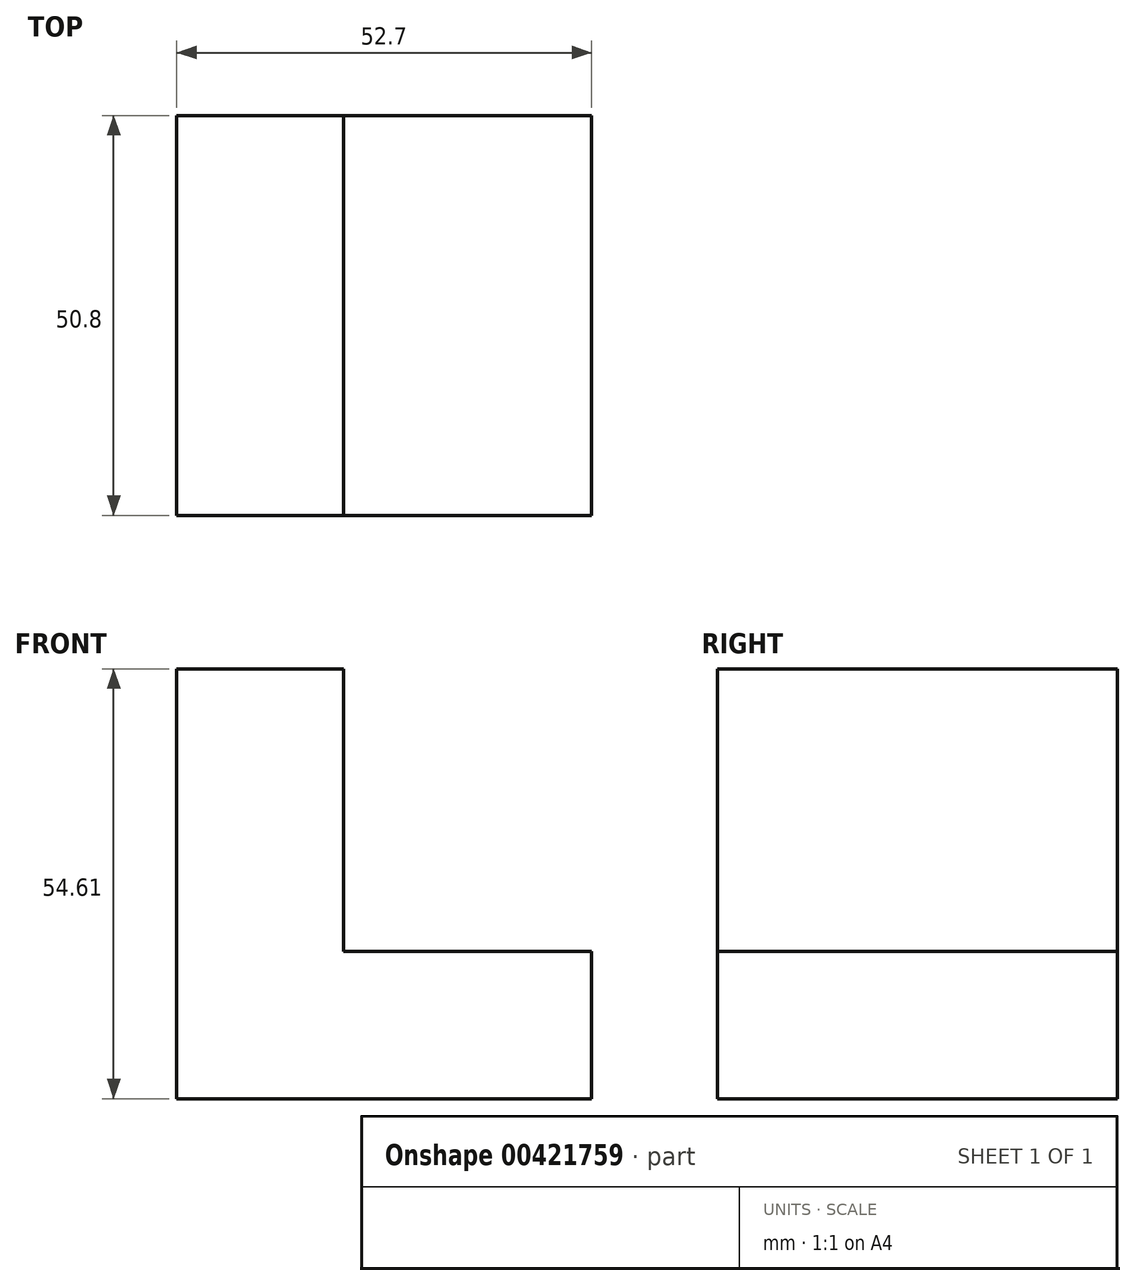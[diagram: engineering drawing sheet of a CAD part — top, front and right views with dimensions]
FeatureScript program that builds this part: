
annotation { "Feature Type Name" : "Feature", "Feature Type Description" : "" }
export const myFeature = defineFeature(function(context is Context, id is Id, definition is map)
    precondition{}
    {
        {
            var Q0;
            Q0=qCreatedBy(makeId("Front.planeOp"),FACE);
            var sketch = newSketch(context, id + "F0", { "sketchPlane" : qUnion([Q0])});
            skLineSegment(sketch, "E0", {"start": v(0, 0) * mm, "end": v(-52.7, 0) * mm});
            skLineSegment(sketch, "E1", {"start": v(-52.7, 0) * mm, "end": v(-52.7, 54.61) * mm});
            skLineSegment(sketch, "E2", {"start": v(-52.7, 54.61) * mm, "end": v(-31.5, 54.61) * mm});
            skLineSegment(sketch, "E3", {"start": v(-31.5, 54.61) * mm, "end": v(-31.5, 18.71) * mm});
            skLineSegment(sketch, "E4", {"start": v(-31.5, 18.71) * mm, "end": v(0, 18.71) * mm});
            skLineSegment(sketch, "E5", {"start": v(0, 18.71) * mm, "end": v(0, 0) * mm});
            skSolve(sketch);
        }
        {
            var Q0;
            Q0 = qSketchRegion(id + "F0", true);
            extrude(context, id + "F1", {"entities" : qUnion([Q0]), "depth" : 50.8 * mm});
        }
    });
